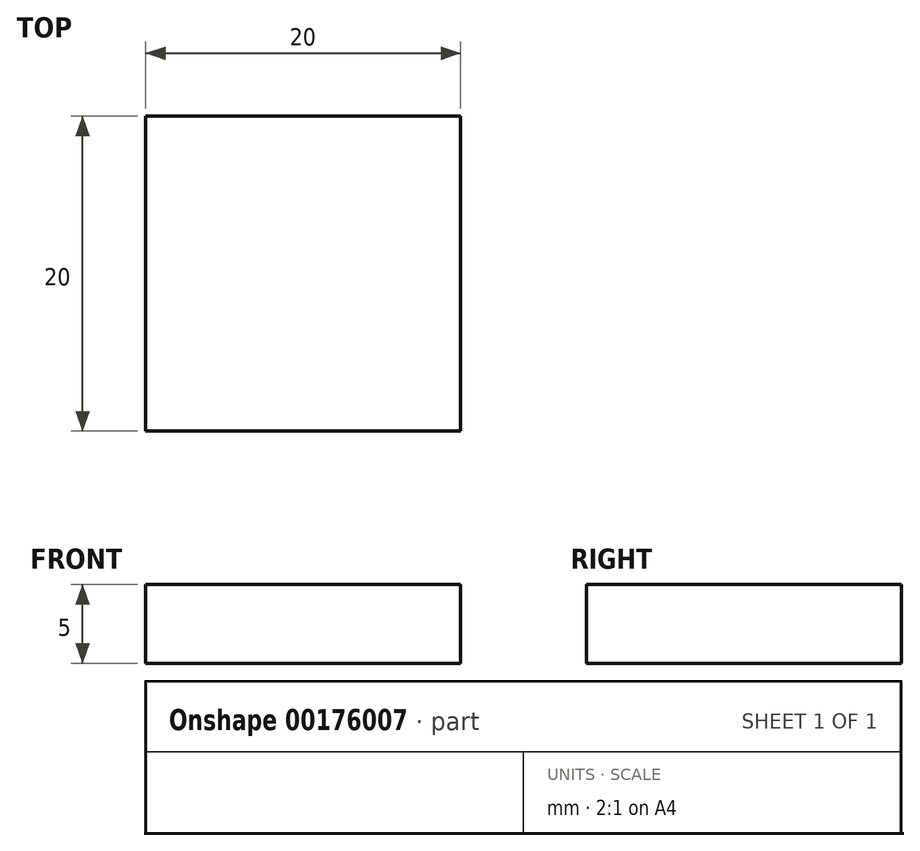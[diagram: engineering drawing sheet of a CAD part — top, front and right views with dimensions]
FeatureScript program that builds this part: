
annotation { "Feature Type Name" : "Feature", "Feature Type Description" : "" }
export const myFeature = defineFeature(function(context is Context, id is Id, definition is map)
    precondition{}
    {
        {
            var Q0;
            Q0=qCreatedBy(makeId("Top.planeOp"),FACE);
            var sketch = newSketch(context, id + "F0", { "sketchPlane" : qUnion([Q0])});
            skLineSegment(sketch, "E0.bottom", {"start": v(10, 10) * mm, "end": v(-10, 10) * mm});
            skLineSegment(sketch, "E0.top", {"start": v(10, -10) * mm, "end": v(-10, -10) * mm});
            skLineSegment(sketch, "E0.left", {"start": v(10, 10) * mm, "end": v(10, -10) * mm});
            skLineSegment(sketch, "E0.right", {"start": v(-10, 10) * mm, "end": v(-10, -10) * mm});
            skPoint(sketch, "E0.middle", {"position": v(0, 0) * mm});
            skSolve(sketch);
        }
        {
            var Q0;
            Q0 = qSketchRegion(id + "F0", true);
            extrude(context, id + "F1", {"entities" : qUnion([Q0]), "depth" : 5 * mm});
        }
    });
